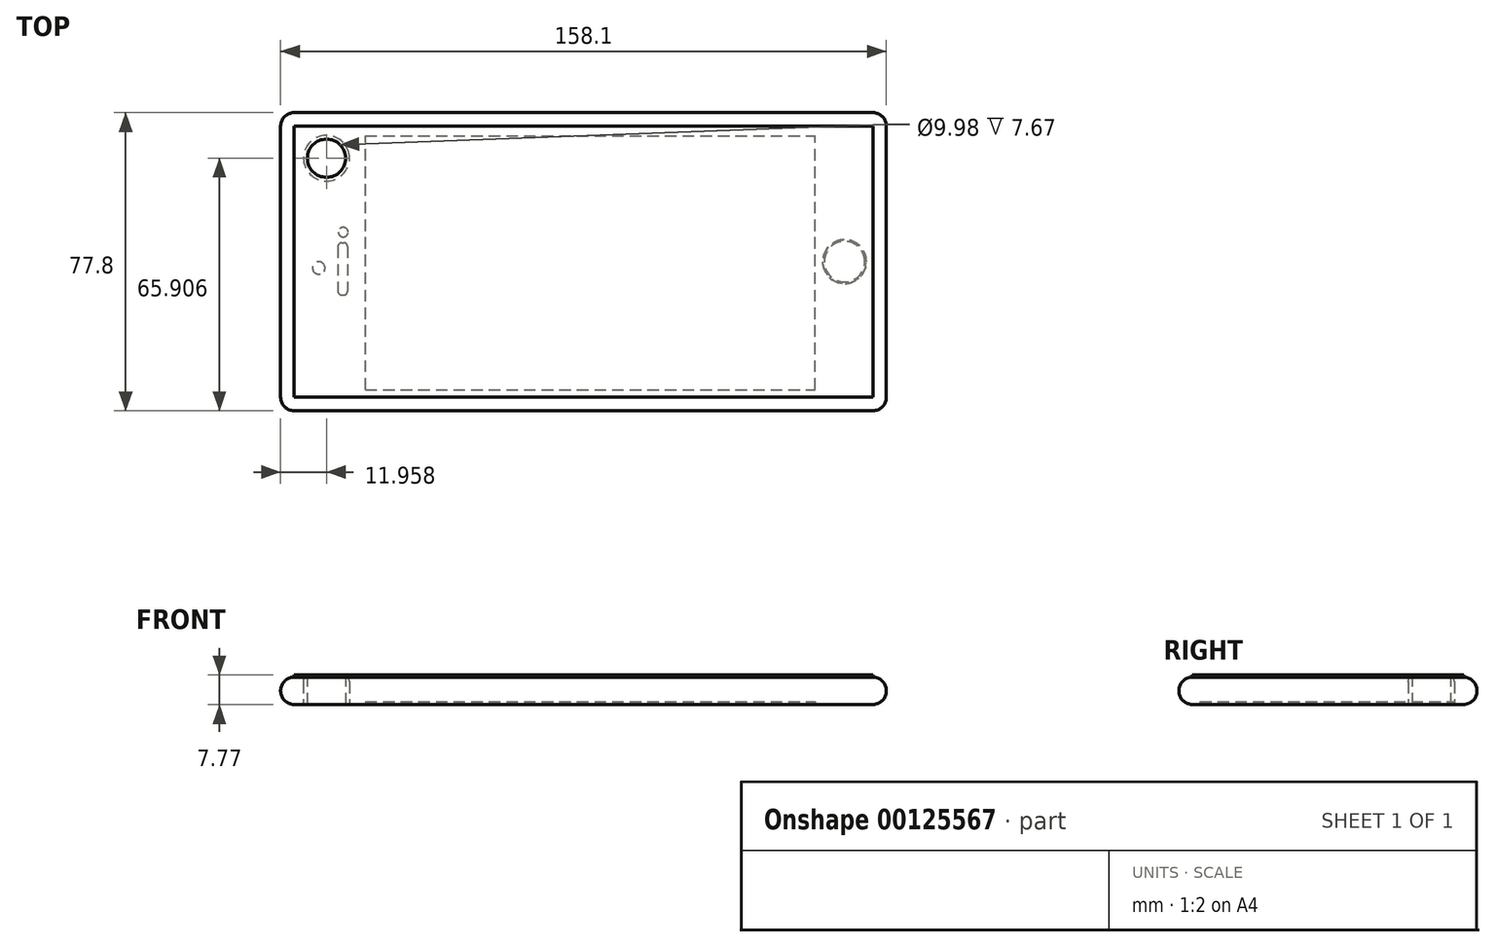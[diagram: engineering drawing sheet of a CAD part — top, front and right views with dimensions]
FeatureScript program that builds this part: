
annotation { "Feature Type Name" : "Feature", "Feature Type Description" : "" }
export const myFeature = defineFeature(function(context is Context, id is Id, definition is map)
    precondition{}
    {
        {
            var Q0;
            Q0=qCreatedBy(makeId("Top.planeOp"),FACE);
            var sketch = newSketch(context, id + "F0", { "sketchPlane" : qUnion([Q0])});
            skLineSegment(sketch, "E0.bottom", {"start": v(0, 0) * mm, "end": v(-158.1, 0) * mm});
            skLineSegment(sketch, "E0.top", {"start": v(0, 77.8) * mm, "end": v(-158.1, 77.8) * mm});
            skLineSegment(sketch, "E0.left", {"start": v(0, 0) * mm, "end": v(0, 77.8) * mm});
            skLineSegment(sketch, "E0.right", {"start": v(-158.1, 0) * mm, "end": v(-158.1, 77.8) * mm});
            skSolve(sketch);
        }
        {
            var Q0;
            Q0 = qSketchRegion(id + "F0", true);
            extrude(context, id + "F1", {"entities" : qUnion([Q0]), "depth" : 7.1 * mm});
        }
        {
            var Q0;
            Q0=makeQuery(id+"F1.opExtrude","CAP_EDGE",EDGE,{"disambiguationData":[OSD([sQuery(id+"F0.wireOp",EDGE,"E0.top")])],"isStart":false});
            var Q1;
            Q1=makeQuery(id+"F1.opExtrude","CAP_EDGE",EDGE,{"disambiguationData":[OSD([sQuery(id+"F0.wireOp",EDGE,"E0.right")])],"isStart":false});
            var Q2;
            Q2=makeQuery(id+"F1.opExtrude","CAP_EDGE",EDGE,{"disambiguationData":[OSD([sQuery(id+"F0.wireOp",EDGE,"E0.right")])],"isStart":true});
            var Q3;
            Q3=makeQuery(id+"F1.opExtrude","CAP_EDGE",EDGE,{"disambiguationData":[OSD([sQuery(id+"F0.wireOp",EDGE,"E0.top")])],"isStart":true});
            var Q4;
            Q4=makeQuery(id+"F1.opExtrude","SWEPT_EDGE",EDGE,{"disambiguationData":[OSD([sQuery(id+"F0.wireOp",EDGE,"E0.top"),sQuery(id+"F0.wireOp",EDGE,"E0.right")])]});
            var Q5;
            Q5=makeQuery(id+"F1.opExtrude","CAP_EDGE",EDGE,{"disambiguationData":[OSD([sQuery(id+"F0.wireOp",EDGE,"E0.left")])],"isStart":false});
            var Q6;
            Q6=makeQuery(id+"F1.opExtrude","CAP_EDGE",EDGE,{"disambiguationData":[OSD([sQuery(id+"F0.wireOp",EDGE,"E0.left")])],"isStart":true});
            var Q7;
            Q7=makeQuery(id+"F1.opExtrude","SWEPT_EDGE",EDGE,{"disambiguationData":[OSD([sQuery(id+"F0.wireOp",EDGE,"E0.top"),sQuery(id+"F0.wireOp",EDGE,"E0.left")])]});
            var Q8;
            Q8=makeQuery(id+"F1.opExtrude","CAP_EDGE",EDGE,{"disambiguationData":[OSD([sQuery(id+"F0.wireOp",EDGE,"E0.bottom")])],"isStart":false});
            var Q9;
            Q9=makeQuery(id+"F1.opExtrude","CAP_EDGE",EDGE,{"disambiguationData":[OSD([sQuery(id+"F0.wireOp",EDGE,"E0.bottom")])],"isStart":true});
            var Q10;
            Q10=makeQuery(id+"F1.opExtrude","SWEPT_EDGE",EDGE,{"disambiguationData":[OSD([sQuery(id+"F0.wireOp",EDGE,"E0.bottom"),sQuery(id+"F0.wireOp",EDGE,"E0.right")])]});
            var Q11;
            Q11=makeQuery(id+"F1.opExtrude","SWEPT_EDGE",EDGE,{"disambiguationData":[OSD([sQuery(id+"F0.wireOp",EDGE,"E0.bottom"),sQuery(id+"F0.wireOp",EDGE,"E0.left")])]});
            fillet(context, id + "F2", {"entities" : qUnion([Q0, Q1, Q2, Q3, Q4, Q5, Q6, Q7, Q8, Q9, Q10, Q11]), "radius" : 3.5 * mm, "tangentPropagation" : true, "allowEdgeOverflow" : false});
        }
        {
            var Q0;
            Q0=qCreatedBy(makeId("Top.planeOp"),FACE);
            var sketch = newSketch(context, id + "F3", { "sketchPlane" : qUnion([Q0])});
            skCircle(sketch, "E1", {"center": v(-146.14, 65.9) * mm, "radius": 5.99 * mm});
            skCircle(sketch, "E2.0", {"center": v(-146.14, 65.9) * mm, "radius": 4.99 * mm});
            skSolve(sketch);
        }
        {
            var Q0;
            Q0=makeQuery(id+"F3.imprint","IMPRINT",FACE,{"disambiguationData":[TD([[makeQuery(id+"F3.imprint","IMPRINT",EDGE,{"derivedFrom":sQuery(id+"F3.wireOp",EDGE,"E1")}),1.0]])]});
            var Q1;
            Q1=makeQuery(id+"F1.opExtrude","CAP_FACE",FACE,{"disambiguationData":[OSD([sQuery(id+"F0.wireOp",EDGE,"E0.bottom"),sQuery(id+"F0.wireOp",EDGE,"E0.top"),sQuery(id+"F0.wireOp",EDGE,"E0.left"),sQuery(id+"F0.wireOp",EDGE,"E0.right")])],"isStart":true});
            extrude(context, id + "F4", {"entities" : qUnion([Q0, Q1]), "depth" : 7.67 * mm, "offsetDistance" : 25 * mm});
        }
        {
            var Q0;
            Q0=makeQuery(id+"F4.opExtrude","CAP_EDGE",EDGE,{"disambiguationData":[OSD([sQuery(id+"F3.wireOp",EDGE,"E1")])],"isStart":false});
            fillet(context, id + "F5", {"entities" : qUnion([Q0]), "radius" : 2 * mm, "tangentPropagation" : true, "allowEdgeOverflow" : false});
        }
        {
            var Q0;
            Q0=makeQuery(id+"F1.opExtrude","CAP_FACE",FACE,{"disambiguationData":[OSD([sQuery(id+"F0.wireOp",EDGE,"E0.bottom"),sQuery(id+"F0.wireOp",EDGE,"E0.top"),sQuery(id+"F0.wireOp",EDGE,"E0.left"),sQuery(id+"F0.wireOp",EDGE,"E0.right")])],"isStart":true});
            var sketch = newSketch(context, id + "F6", { "sketchPlane" : qUnion([Q0])});
            skLineSegment(sketch, "E3.bottom", {"start": v(-135.97, -5.52) * mm, "end": v(-18.56, -5.52) * mm});
            skLineSegment(sketch, "E3.top", {"start": v(-135.97, -71.8) * mm, "end": v(-18.56, -71.8) * mm});
            skLineSegment(sketch, "E3.left", {"start": v(-135.97, -5.52) * mm, "end": v(-135.97, -71.8) * mm});
            skLineSegment(sketch, "E3.right", {"start": v(-18.56, -5.52) * mm, "end": v(-18.56, -71.8) * mm});
            skSolve(sketch);
        }
        {
            var Q0;
            Q0 = qSketchRegion(id + "F6", true);
            extrude(context, id + "F7", {"entities" : qUnion([Q0]), "operationType" : NewBodyOperationType.REMOVE, "oppositeDirection" : true, "depth" : .75 * mm});
        }
        {
            var Q0;
            Q0=makeQuery(id+"F1.opExtrude","CAP_FACE",FACE,{"disambiguationData":[OSD([sQuery(id+"F0.wireOp",EDGE,"E0.bottom"),sQuery(id+"F0.wireOp",EDGE,"E0.top"),sQuery(id+"F0.wireOp",EDGE,"E0.left"),sQuery(id+"F0.wireOp",EDGE,"E0.right")])],"isStart":true});
            var sketch = newSketch(context, id + "F8", { "sketchPlane" : qUnion([Q0])});
            skCircle(sketch, "E4", {"center": v(-148.15, -37.25) * mm, "radius": 1.63 * mm});
            skPoint(sketch, "E4.centerSnap0", {"position": v(-135.97, -38.65) * mm});
            skCircle(sketch, "E5", {"center": v(-141.76, -46.6) * mm, "radius": 1.25 * mm});
            skLineSegment(sketch, "E6.bottom", {"start": v(-142.13, -43.84) * mm, "end": v(-141.63, -43.84) * mm});
            skLineSegment(sketch, "E6.top", {"start": v(-142.13, -30.18) * mm, "end": v(-141.63, -30.18) * mm});
            skLineSegment(sketch, "E6.left", {"start": v(-143.13, -42.84) * mm, "end": v(-143.13, -31.18) * mm});
            skLineSegment(sketch, "E6.right", {"start": v(-140.63, -42.84) * mm, "end": v(-140.63, -31.18) * mm});
            skPoint(sketch, "E7.visualSharp", {"position": v(-143.13, -30.18) * mm});
            skArc(sketch, "E7.filletArc", {"start": v(-142.13, -30.18) * mm, "mid": v(-142.84, -30.47) * mm, "end": v(-143.13, -31.18) * mm});
            skPoint(sketch, "E8.visualSharp", {"position": v(-140.63, -30.18) * mm});
            skArc(sketch, "E8.filletArc", {"start": v(-140.63, -31.18) * mm, "mid": v(-140.93, -30.47) * mm, "end": v(-141.63, -30.18) * mm});
            skPoint(sketch, "E9.visualSharp", {"position": v(-143.13, -43.84) * mm});
            skArc(sketch, "E9.filletArc", {"start": v(-143.13, -42.84) * mm, "mid": v(-142.84, -43.55) * mm, "end": v(-142.13, -43.84) * mm});
            skPoint(sketch, "E10.visualSharp", {"position": v(-140.63, -43.84) * mm});
            skArc(sketch, "E10.filletArc", {"start": v(-141.63, -43.84) * mm, "mid": v(-140.93, -43.55) * mm, "end": v(-140.63, -42.84) * mm});
            skSolve(sketch);
        }
        {
            var Q0;
            Q0=makeQuery(id+"F8.imprint","IMPRINT",FACE,{"disambiguationData":[TD([[makeQuery(id+"F8.imprint","IMPRINT",EDGE,{"derivedFrom":sQuery(id+"F8.wireOp",EDGE,"E6.bottom")}),1.0]])]});
            var Q1;
            Q1=makeQuery(id+"F8.imprint","IMPRINT",FACE,{"disambiguationData":[TD([[makeQuery(id+"F8.imprint","IMPRINT",EDGE,{"derivedFrom":sQuery(id+"F8.wireOp",EDGE,"E5")}),1.0]])]});
            var Q2;
            Q2=makeQuery(id+"F8.imprint","IMPRINT",FACE,{"disambiguationData":[TD([[makeQuery(id+"F8.imprint","IMPRINT",EDGE,{"derivedFrom":sQuery(id+"F8.wireOp",EDGE,"E4")}),1.0]])]});
            var Q3;
            Q3=sQuery(id+"F8.wireOp",EDGE,"E6.left");
            var Q4;
            Q4=sQuery(id+"F8.wireOp",EDGE,"E6.right");
            var Q5;
            Q5=sQuery(id+"F8.wireOp",EDGE,"E7.filletArc");
            var Q6;
            Q6=sQuery(id+"F8.wireOp",EDGE,"E8.filletArc");
            var Q7;
            Q7=sQuery(id+"F8.wireOp",EDGE,"E5");
            var Q8;
            Q8=sQuery(id+"F8.wireOp",EDGE,"E4");
            extrude(context, id + "F9", {"entities" : qUnion([Q0, Q1, Q2]), "operationType" : NewBodyOperationType.ADD, "surfaceEntities" : qUnion([Q3, Q4, Q5, Q6, Q7, Q8]), "depth" : .1 * mm});
        }
        {
            var Q0;
            Q0=makeQuery(id+"F1.opExtrude","CAP_FACE",FACE,{"disambiguationData":[OSD([sQuery(id+"F0.wireOp",EDGE,"E0.bottom"),sQuery(id+"F0.wireOp",EDGE,"E0.top"),sQuery(id+"F0.wireOp",EDGE,"E0.left"),sQuery(id+"F0.wireOp",EDGE,"E0.right")])],"isStart":true});
            var sketch = newSketch(context, id + "F10", { "sketchPlane" : qUnion([Q0])});
            skCircle(sketch, "E11", {"center": v(-10.91, -38.9) * mm, "radius": 5.98 * mm});
            skPoint(sketch, "E11.centerSnap0", {"position": v(-3.5, -38.9) * mm});
            skCircle(sketch, "E12.0", {"center": v(-10.91, -38.9) * mm, "radius": 4.95 * mm});
            skSolve(sketch);
        }
        {
            var Q0;
            Q0=makeQuery(id+"F10.imprint","IMPRINT",FACE,{"disambiguationData":[TD([[makeQuery(id+"F10.imprint","IMPRINT",EDGE,{"derivedFrom":sQuery(id+"F10.wireOp",EDGE,"E11")}),1.0]])]});
            var Q1;
            Q1=sQuery(id+"F10.wireOp",EDGE,"E11");
            extrude(context, id + "F11", {"entities" : qUnion([Q0]), "operationType" : NewBodyOperationType.REMOVE, "surfaceEntities" : qUnion([Q1]), "endBound" : BoundingType.SYMMETRIC, "depth" : 0.25 * mm});
        }
        {
            var Q0;
            Q0=makeQuery(id+"F11.boolean.opBoolean","COPY",FACE,{"derivedFrom":makeQuery(id+"F11.opExtrude","CAP_FACE",FACE,{"disambiguationData":[OSD([sQuery(id+"F10.wireOp",EDGE,"E11"),sQuery(id+"F10.wireOp",EDGE,"E12.0")])],"isStart":true})});
            chamfer(context, id + "F12", {"entities" : qUnion([Q0]), "width" : 0.35 * mm, "tangentPropagation" : true});
        }
        {
            var Q0;
            Q0=makeQuery(id+"F11.boolean.opBoolean","SPLIT",FACE,{"disambiguationData":[TD([makeQuery(id+"F11.opExtrude","SWEPT_FACE",FACE,{"disambiguationData":[OSD([sQuery(id+"F10.wireOp",EDGE,"E12.0")])]})])],"derivedFrom":makeQuery(id+"F1.opExtrude","CAP_FACE",FACE,{"disambiguationData":[OSD([sQuery(id+"F0.wireOp",EDGE,"E0.bottom"),sQuery(id+"F0.wireOp",EDGE,"E0.top"),sQuery(id+"F0.wireOp",EDGE,"E0.left"),sQuery(id+"F0.wireOp",EDGE,"E0.right")])],"isStart":true})});
            fillet(context, id + "F13", {"entities" : qUnion([Q0]), "radius" : .25 * mm, "tangentPropagation" : true, "allowEdgeOverflow" : false});
        }
    });
